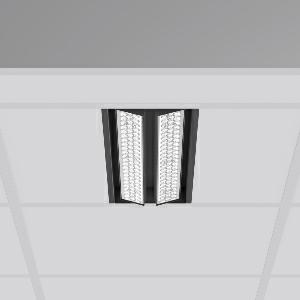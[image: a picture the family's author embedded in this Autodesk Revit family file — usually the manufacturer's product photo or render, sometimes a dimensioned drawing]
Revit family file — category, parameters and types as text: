
# Revit family: tx-move_901737_003_3_76_ef29
name_source: partatom
category: Lighting Fixtures
units: mm (PartAtom-declared; Revit-internal decimal feet)

## family parameters
Cut with Voids When Loaded = No
Host = Face
Light Source = No
Part Type = Normal
Room Calculation Point = No
Round Connector Dimension = Use Diameter
Shared = No

## types (1)
- MultiLumen 1 (1 x LED Modul 835, 2825 lm, 3500)
    Apparent Load = 35 VA
    CIE Flux Codes = 77 96 99 100 100
    Color Rendering = 80
    Color Temperature = 3500
    Default Elevation = 1800 mm
    Description = Series: TX-MOVE
Einlege/Einbau-Flächenstrahler. Housing: sheet steel, powder-coated. 2xSwivel range: 90°. High-efficiency LED units with optimum light control thanks to clear plastic (PC) lens optics. Spezielle Mikrostrukturen reduzieren Gelbsaum. Symmetrical light distribution. Suitable for laying in grid ceiling module 625. Connected converter included in separate gearbox.Suitable for through-wiring.MultiLumen: Luminous flux adjustable in 3 steps. Accessories: Mounting frame for installation in suspended ceilings. Environmentally friendly and resource-saving due to replaceable and recyclable components. 
Colour: deep black, matt (RAL 9005)
Length: 622 mm
Width: 190 mm
Height: 39 mm
Cut-out length: 602 mm
Cut-out width: 174 mm
Recess height: 100 mm
Lamp: LED
Socket: without socket
Colour temperature: 3500K
Colour rendering index (CRI): 80
System power: 35 W
Rated luminous flux: 5650 lm
Luminous efficiency: 161 lm/W
System power 2: 47 W
Rated luminous flux 2: 7350 lm
Luminous efficiency 2: 156 lm/W
System power 3: 68 W
Rated luminous flux 3: 10000 lm
Luminous efficiency 3: 147 lm/W
Control gear: Dimmable EVG, DALI
Protection class: I
Type of protection: IP 20
    Height = 0 mm  [stored 0 ft]
    Lamp = 1 x LED Modul 835
    Lamp Light Flux = 2825 lm
    Lamp count = 1
    Length = 622 mm
    Lifetime = 50000 h
    Luminous efficacy = 161 lm/W
    Manufacturer = RZB
    ModVariant = No
    Model = 901737.003.3.76
    Mounting Place = Ceiling, Wall
    Mounting Type = Recessed
    Number of Poles = 1
    OnlyDefault = Yes
    Power Factor = 1
    Product Name = TX-MOVE
    Product group = Recessed projectors
    ProductGroupID = 401
    Protection Class = Protection class I
    Protection Degree = IP 20
    RLX_Detail_Level = 1
    RLX_Emergency_Light_Flux = 0 lm
    RLX_Emergency_Type = 0
    RLX_Emergency_Type_DB = No
    RlxData = <blob elided: 35713 chars, md5=5cc0cfa3>
    Socket = socket
    Standby Power = 0 W
    System Light Flux = 5650 lm
    System Power = 35 W
    Type Comments = MultiLumen 1
    Type Image = 901737.003.jpg
    URL = http://relux.com
    VarID = multilumen_1
    Voltage = 230 V
    Voltage Range = 220-240 V
    Weight = 0.00 kg
    Width = 190 mm  [stored 0.62336 ft]

note: [stored X ft] marks values corroborated as IEEE doubles in the binary element streams (Revit-internal decimal feet)

## geometry (parser evidence)
native form markers: Blend x4, Sweep x14
no freeform markers — native parametric forms only
